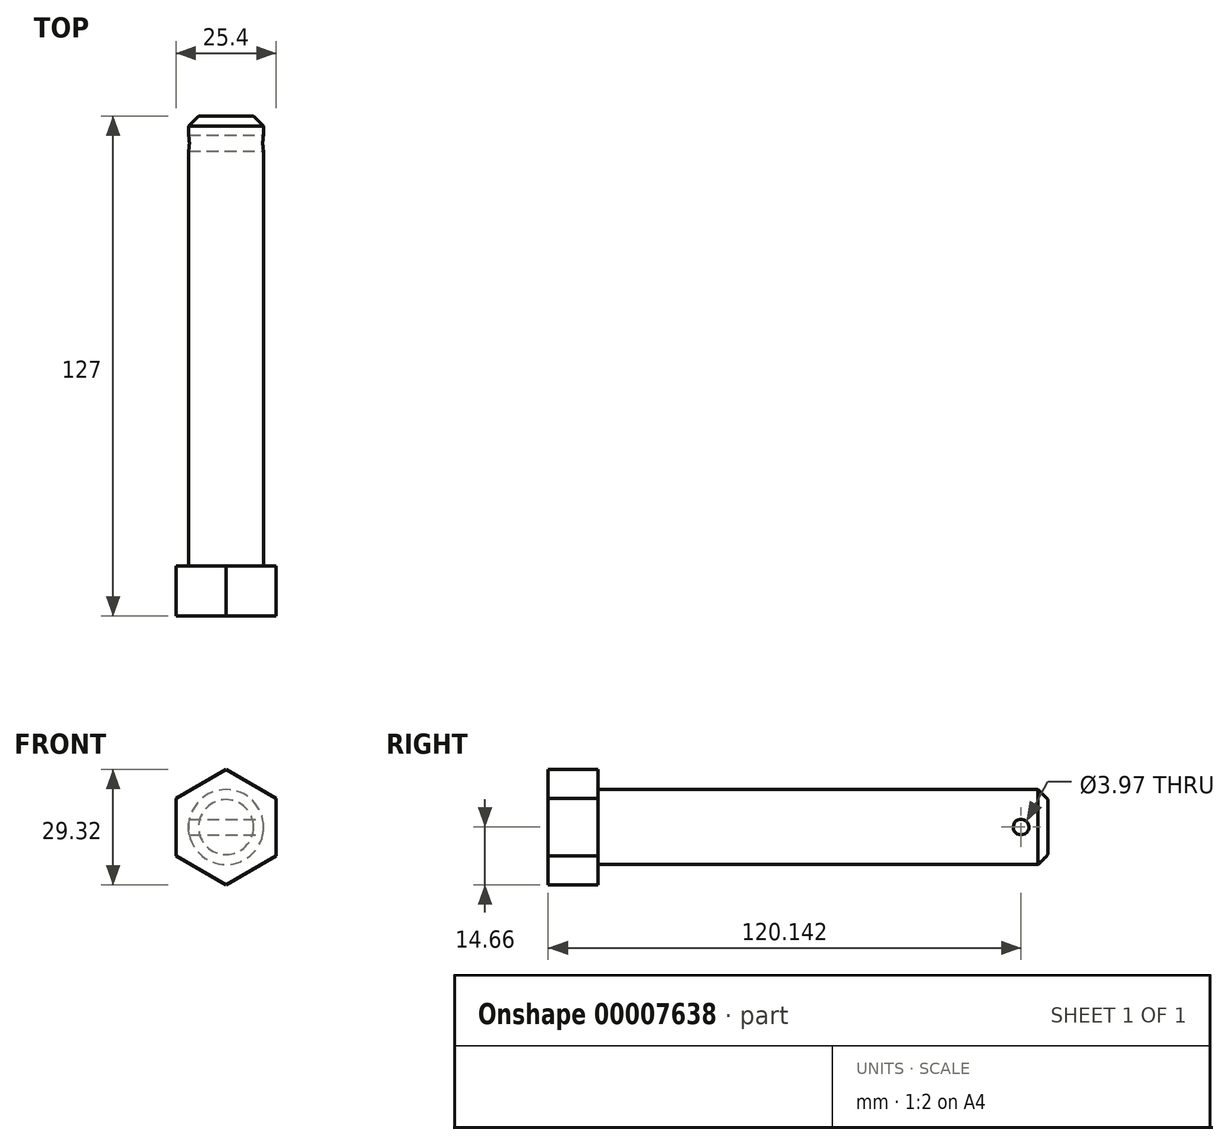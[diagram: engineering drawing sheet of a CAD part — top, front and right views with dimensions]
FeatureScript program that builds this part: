
annotation { "Feature Type Name" : "Feature", "Feature Type Description" : "" }
export const myFeature = defineFeature(function(context is Context, id is Id, definition is map)
    precondition{}
    {
        {
            var Q0;
            Q0=qCreatedBy(makeId("Front.planeOp"),FACE);
            var sketch = newSketch(context, id + "F0", { "sketchPlane" : qUnion([Q0])});
            skCircle(sketch, "E0", {"center": v(0, 0) * mm, "radius": 9.53 * mm});
            skSolve(sketch);
        }
        {
            var Q0;
            Q0 = qSketchRegion(id + "F0", true);
            extrude(context, id + "F1", {"entities" : qUnion([Q0]), "depth" : 114.3 * mm, "symmetric" : true});
        }
        {
            var Q0;
            Q0=makeQuery(id+"F1.opExtrude","CAP_FACE",FACE,{"disambiguationData":[OSD([sQuery(id+"F0.wireOp",EDGE,"E0")])],"isStart":false});
            var sketch = newSketch(context, id + "F2", { "sketchPlane" : qUnion([Q0])});
            skCircle(sketch, "E1.cCircle", {"center": v(0, 0) * mm, "radius": 12.7 * mm, "construction": true});
            skLineSegment(sketch, "E1.0", {"start": v(-12.7, -7.33) * mm, "end": v(-12.7, 7.33) * mm});
            skLineSegment(sketch, "E1.1", {"start": v(-12.7, 7.33) * mm, "end": v(0, 14.66) * mm});
            skLineSegment(sketch, "E1.2", {"start": v(0, 14.66) * mm, "end": v(12.7, 7.33) * mm});
            skLineSegment(sketch, "E1.3", {"start": v(12.7, 7.33) * mm, "end": v(12.7, -7.33) * mm});
            skLineSegment(sketch, "E1.4", {"start": v(12.7, -7.33) * mm, "end": v(0, -14.66) * mm});
            skLineSegment(sketch, "E1.5", {"start": v(0, -14.66) * mm, "end": v(-12.7, -7.33) * mm});
            skPoint(sketch, "E1.0.midPoint", {"position": v(-12.7, 0) * mm});
            skSolve(sketch);
        }
        {
            var Q0;
            Q0 = qSketchRegion(id + "F2", true);
            extrude(context, id + "F3", {"entities" : qUnion([Q0]), "operationType" : NewBodyOperationType.ADD, "depth" : 12.7 * mm});
        }
        {
            var Q0;
            Q0=makeQuery(id+"F1.opExtrude","CAP_EDGE",EDGE,{"disambiguationData":[OSD([sQuery(id+"F0.wireOp",EDGE,"E0")])],"isStart":true});
            chamfer(context, id + "F4", {"entities" : qUnion([Q0]), "width" : 2.54 * mm, "tangentPropagation" : true});
        }
        {
            var Q0;
            Q0=qCreatedBy(makeId("Right.planeOp"),FACE);
            var sketch = newSketch(context, id + "F5", { "sketchPlane" : qUnion([Q0])});
            skCircle(sketch, "E2", {"center": v(50.3, 0) * mm, "radius": 1.98 * mm});
            skSolve(sketch);
        }
        {
            var Q0;
            Q0 = qSketchRegion(id + "F5", true);
            extrude(context, id + "F6", {"entities" : qUnion([Q0]), "operationType" : NewBodyOperationType.REMOVE, "oppositeDirection" : true, "depth" : 50.8 * mm, "symmetric" : true});
        }
    });
